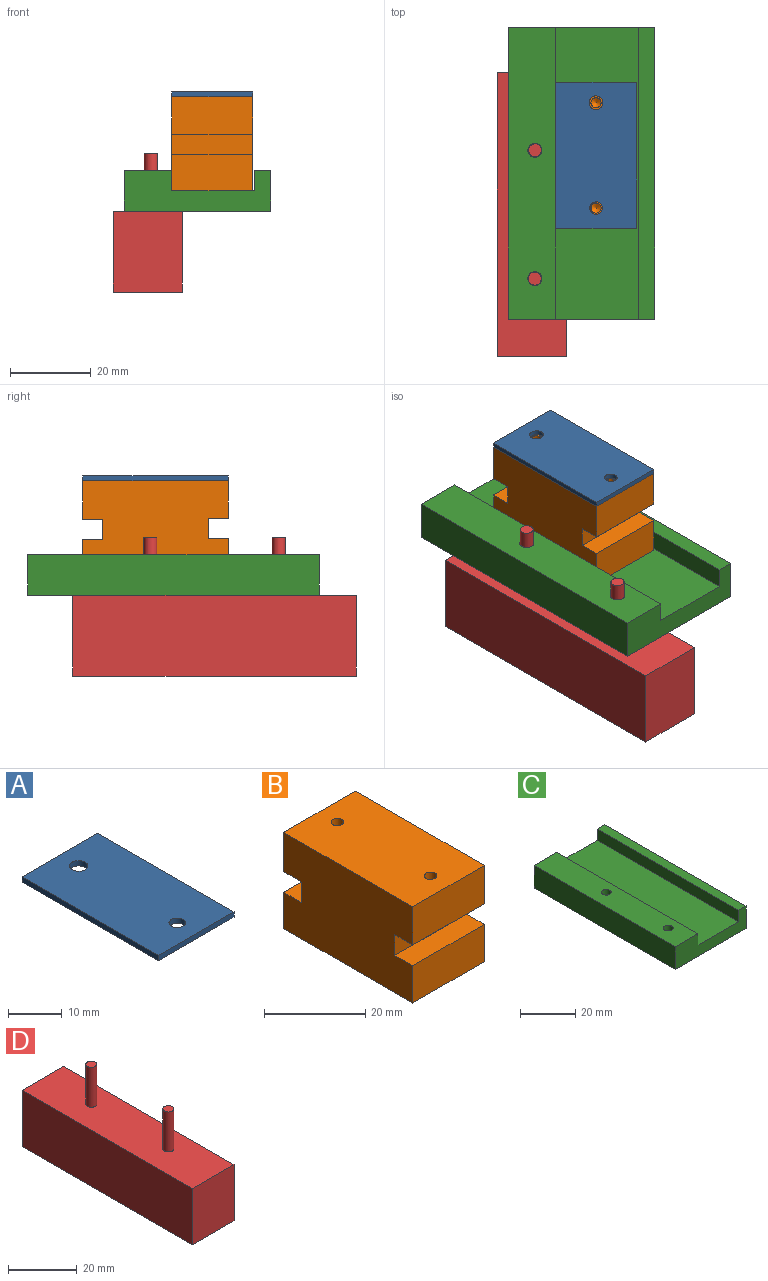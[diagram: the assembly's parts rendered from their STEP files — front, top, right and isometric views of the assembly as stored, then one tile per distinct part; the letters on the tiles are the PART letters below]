
ASSEMBLY  parts=4 mates=6
PART A: 8 faces, bbox 20x36x1.2 mm
  f0: plane 36x1.2mm, normal (-1,0,0), area 43.2mm2, adj f1,f3,f4,f5
  f1: plane 36x20mm, normal (0,0,-1), area 703.5mm2, adj f0,f2,f4,f5,f6,f7
  f2: plane 36x1.2mm, normal (1,0,0), area 43.2mm2, adj f1,f3,f4,f5
  f3: plane 36x20mm, normal (0,0,1), area 703.5mm2, adj f0,f2,f4,f5,f6,f7
  f4: plane 20x1.2mm, normal (0,-1,0), area 24mm2, adj f0,f1,f2,f3
  f5: plane 20x1.2mm, normal (0,1,0), area 24mm2, adj f0,f1,f2,f3
  f6: cylinder r=1.54mm len=3.08mm, axis (0,0,1), area 11.6mm2, adj f1,f3
  f7: cylinder r=1.7mm len=3.4mm, axis (0,0,1), area 12.8mm2, adj f1,f3
PART B: 22 faces, bbox 20x36x23.3 mm
  f0: plane 20x9.5mm, normal (0,1,0), area 190mm2, adj f1,f4,f5,f11
  f1: plane 36x23.25mm, normal (-1,0,0), area 787mm2, adj f0,f2,f3,f5,f6,f7,f8,f9
  f2: plane 20x9.25mm, normal (0,-1,0), area 185mm2, adj f1,f4,f5,f8
  f3: plane 36x20mm, normal (0,0,-1), area 710.2mm2, adj f1,f4,f6,f7,f19,f21
  f4: plane 36x23.25mm, normal (1,0,0), area 787mm2, adj f0,f2,f3,f5,f6,f7,f8,f9
  f5: plane 36x20mm, normal (0,0,1), area 710.2mm2, adj f0,f1,f2,f4,f15,f17
  f6: plane 20x9mm, normal (0,-1,0), area 180mm2, adj f1,f3,f4,f9
  f7: plane 20x8.75mm, normal (0,1,0), area 175mm2, adj f1,f3,f4,f12
  f8: plane 20x5mm, normal (0,0,-1), area 100mm2, adj f1,f2,f4,f10
  f9: plane 20x5mm, normal (0,0,1), area 100mm2, adj f1,f4,f6,f10
  f10: plane 20x5mm, normal (0,-1,0), area 100mm2, adj f1,f4,f8,f9
  f11: plane 20x5mm, normal (0,0,-1), area 100mm2, adj f0,f1,f4,f13
  f12: plane 20x5mm, normal (0,0,1), area 100mm2, adj f1,f4,f7,f13
  f13: plane 20x5mm, normal (0,1,0), area 100mm2, adj f1,f4,f11,f12
  f14: cone r=0mm half-angle=59deg, axis (0,0,1), area 5.7mm2, adj f15
  f15: cylinder r=1.25mm len=6.5mm, axis (0,0,1), area 51.1mm2, adj f5,f14
  f16: cone r=0mm half-angle=59deg, axis (0,0,1), area 5.7mm2, adj f17
  f17: cylinder r=1.25mm len=6.5mm, axis (0,0,1), area 51.1mm2, adj f5,f16
  f18: cone r=0mm half-angle=59deg, axis (0,0,-1), area 5.7mm2, adj f19
  f19: cylinder r=1.25mm len=6.5mm, axis (0,0,-1), area 51.1mm2, adj f3,f18
  f20: cone r=0mm half-angle=59deg, axis (0,0,-1), area 5.7mm2, adj f21
  f21: cylinder r=1.25mm len=6.5mm, axis (0,0,-1), area 51.1mm2, adj f3,f20
PART C: 12 faces, bbox 36.2x72x10 mm
  f0: plane 72x10mm, normal (-1,0,0), area 720mm2, adj f2,f6,f10,f11
  f1: plane 72x10mm, normal (1,0,0), area 720mm2, adj f3,f6,f10,f11
  f2: plane 72x11.7mm, normal (0,0,1), area 823.2mm2, adj f0,f5,f8,f9,f10,f11
  f3: plane 72x4mm, normal (0,0,1), area 288mm2, adj f1,f4,f10,f11
  f4: plane 72x5mm, normal (-1,0,0), area 360mm2, adj f3,f7,f10,f11
  f5: plane 72x5mm, normal (1,0,0), area 360mm2, adj f2,f7,f10,f11
  f6: plane 72x36.2mm, normal (0,0,-1), area 2587.2mm2, adj f0,f1,f8,f9,f10,f11
  f7: plane 72x20.5mm, normal (0,0,1), area 1476mm2, adj f4,f5,f10,f11
  f8: cylinder r=1.75mm len=10mm, axis (0,0,-1), area 110mm2, adj f2,f6
  f9: cylinder r=1.75mm len=10mm, axis (0,0,-1), area 110mm2, adj f2,f6
  f10: plane 36.2x10mm, normal (0,-1,0), area 259.5mm2, adj f0,f1,f2,f3,f4,f5,f6,f7
  f11: plane 36.2x10mm, normal (0,1,0), area 259.5mm2, adj f0,f1,f2,f3,f4,f5,f6,f7
PART D: 10 faces, bbox 17.1x70x34.2 mm
  f0: plane 20x17.1mm, normal (0,1,0), area 342mm2, adj f1,f3,f4,f7
  f1: plane 70x20mm, normal (-1,0,0), area 1400mm2, adj f0,f2,f4,f7
  f2: plane 20x17.1mm, normal (0,-1,0), area 342mm2, adj f1,f3,f4,f7
  f3: plane 70x20mm, normal (1,0,0), area 1400mm2, adj f0,f2,f4,f7
  f4: plane 70x17.1mm, normal (0,0,-1), area 1197mm2, adj f0,f1,f2,f3
  f5: cylinder r=1.61mm len=14.2mm, axis (0,0,1), area 143.7mm2, adj f7,f8
  f6: cylinder r=1.6mm len=14.2mm, axis (0,0,1), area 142.8mm2, adj f7,f9
  f7: plane 70x17.1mm, normal (0,0,1), area 1180.8mm2, adj f0,f1,f2,f3,f5,f6
  f8: plane 3.22x3.22mm, normal (0,0,1), area 8.1mm2, adj f5
  f9: plane 3.2x3.2mm, normal (0,0,1), area 8mm2, adj f6
PLACE A t=(-14.39,8.59,33.11)mm
PLACE B t=(-14.39,8.59,9.86)mm
PLACE C t=(-26.09,28.53,4.86)mm
PLACE D t=(-19.49,-23.97,-15.14)mm
MATE cylindrical D.f5 <-> C.f9  axis (0,0,1) through (-19.49,-39.82,11.96)mm
MATE cylindrical A.f6 <-> B.f14  axis (0,0,-1) through (-4.39,-22.41,33.11)mm
MATE planar B.f1 <-> C.f5  axis (-1,0,0) through (-14.39,-9.41,33.11)mm
MATE planar B.f3 <-> C.f7  axis (0,0,-1) through (-4.39,-9.41,9.86)mm
MATE planar A.f1 <-> B.f5  axis (0,0,-1) through (-4.39,-9.44,33.11)mm
MATE planar C.f6 <-> D.f7  axis (0,0,-1) through (-7.91,-13.74,4.86)mm
